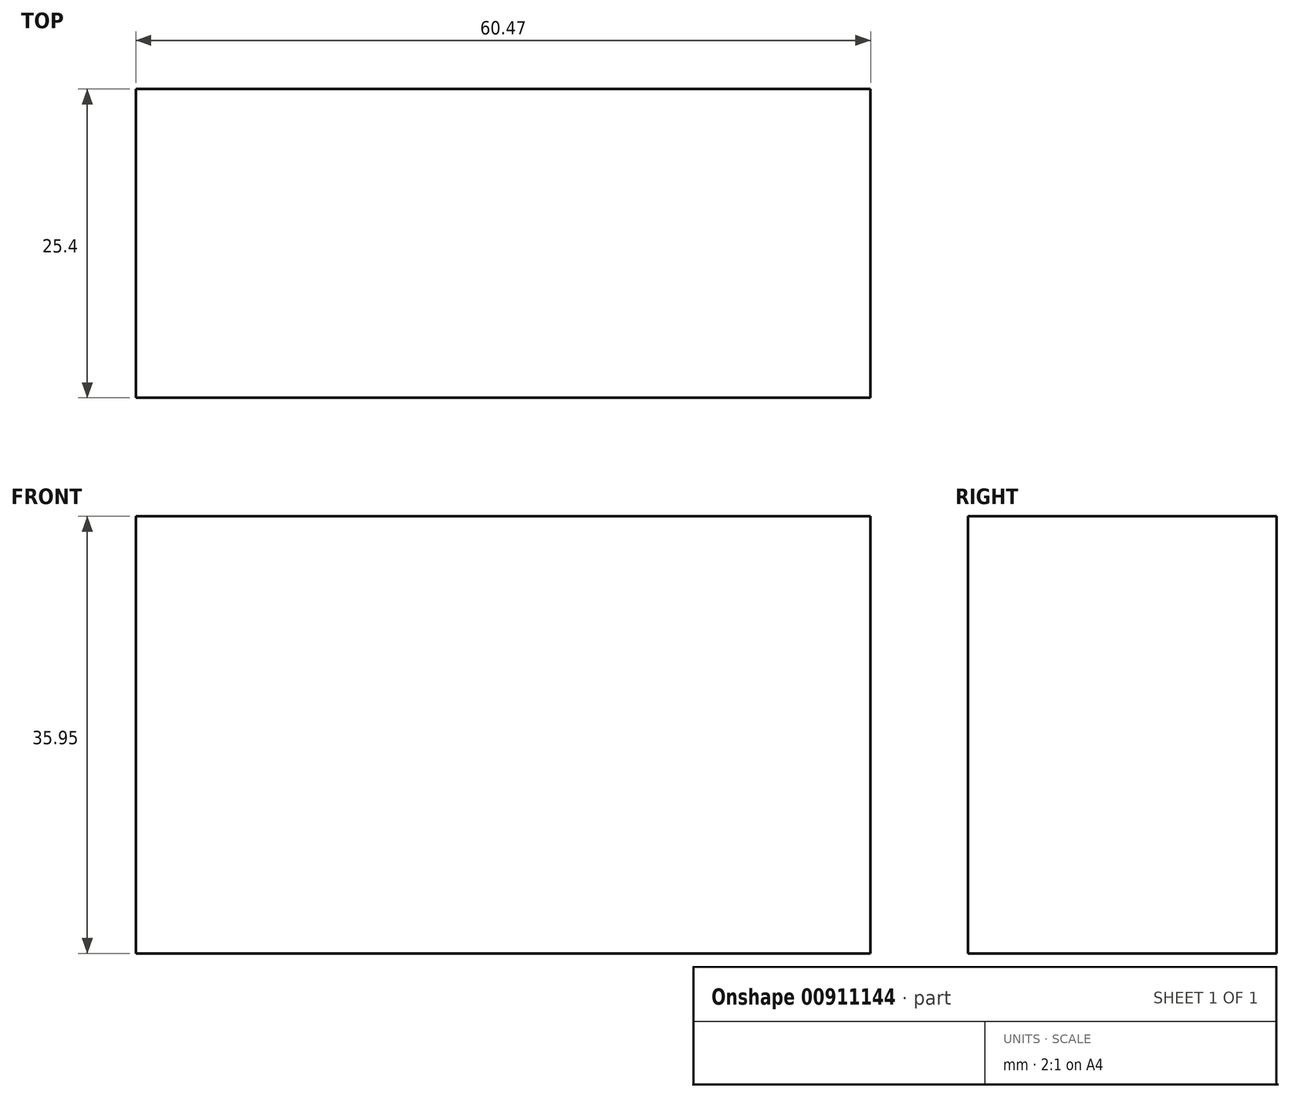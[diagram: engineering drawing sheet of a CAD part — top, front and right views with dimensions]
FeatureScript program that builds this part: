
annotation { "Feature Type Name" : "Feature", "Feature Type Description" : "" }
export const myFeature = defineFeature(function(context is Context, id is Id, definition is map)
    precondition{}
    {
        {
            var Q0;
            Q0=qCreatedBy(makeId("Front.planeOp"),FACE);
            var sketch = newSketch(context, id + "F0", { "sketchPlane" : qUnion([Q0])});
            skLineSegment(sketch, "E0", {"start": v(-127.48, -15.58) * mm, "end": v(-100.38, 32.17) * mm});
            skLineSegment(sketch, "E1.bottom", {"start": v(-74.2, 20.19) * mm, "end": v(-13.73, 20.19) * mm});
            skLineSegment(sketch, "E1.top", {"start": v(-74.2, -15.76) * mm, "end": v(-13.73, -15.76) * mm});
            skLineSegment(sketch, "E1.left", {"start": v(-74.2, 20.19) * mm, "end": v(-74.2, -15.76) * mm});
            skLineSegment(sketch, "E1.right", {"start": v(-13.73, 20.19) * mm, "end": v(-13.73, -15.76) * mm});
            skCircle(sketch, "E2", {"center": v(47.47, 35.12) * mm, "radius": 18.96 * mm});
            skSolve(sketch);
        }
        {
            var Q0;
            Q0=makeQuery(id+"F0.imprint","IMPRINT",FACE,{"disambiguationData":[TD([[makeQuery(id+"F0.imprint","IMPRINT",EDGE,{"derivedFrom":sQuery(id+"F0.wireOp",EDGE,"E1.bottom")}),-1.0]])]});
            extrude(context, id + "F1", {"entities" : qUnion([Q0]), "depth" : 25.4 * mm, "offsetDistance" : 25.4 * mm});
        }
    });
